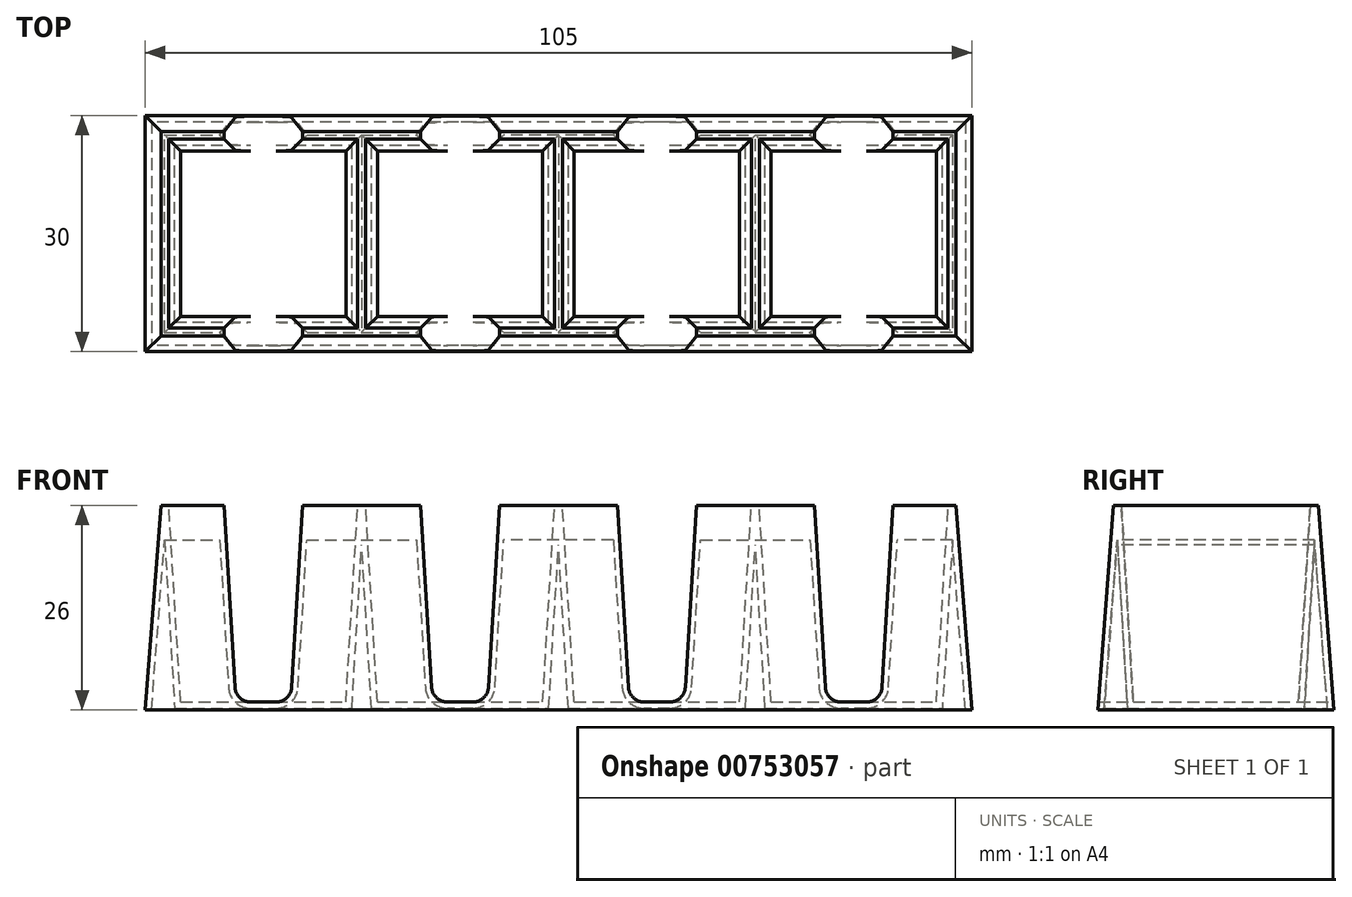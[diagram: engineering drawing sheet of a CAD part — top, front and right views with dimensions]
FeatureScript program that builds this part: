
annotation { "Feature Type Name" : "Feature", "Feature Type Description" : "" }
export const myFeature = defineFeature(function(context is Context, id is Id, definition is map)
    precondition{}
    {
        {
            var Q0;
            Q0=qCreatedBy(makeId("Right.planeOp"),FACE);
            var sketch = newSketch(context, id + "F0", { "sketchPlane" : qUnion([Q0])});
            skLineSegment(sketch, "E0.bottom", {"start": v(15, 0) * mm, "end": v(-15, 0) * mm});
            skLineSegment(sketch, "E0.top", {"start": v(13, 26) * mm, "end": v(-13, 26) * mm});
            skLineSegment(sketch, "E0.left", {"start": v(15, 0) * mm, "end": v(13, 26) * mm});
            skLineSegment(sketch, "E0.right", {"start": v(-15, 0) * mm, "end": v(-13, 26) * mm});
            skPoint(sketch, "E1", {"position": v(0, 26) * mm});
            skSolve(sketch);
        }
        {
            var Q0;
            Q0=makeQuery(id+"F0.imprint","IMPRINT",FACE,{"disambiguationData":[TD([[makeQuery(id+"F0.imprint","IMPRINT",EDGE,{"derivedFrom":sQuery(id+"F0.wireOp",EDGE,"E0.bottom")}),-1.0]])]});
            extrude(context, id + "F1", {"entities" : qUnion([Q0]), "depth" : 105 * mm, "offsetDistance" : 25 * mm});
        }
        {
            var Q0;
            Q0=qCreatedBy(makeId("Front.planeOp"),FACE);
            var sketch = newSketch(context, id + "F2", { "sketchPlane" : qUnion([Q0])});
            skLineSegment(sketch, "E2.0.0", {"start": v(0, 0) * mm, "end": v(0, 26) * mm});
            skLineSegment(sketch, "E2.0.1", {"start": v(0, 26) * mm, "end": v(105, 26) * mm});
            skLineSegment(sketch, "E2.0.2", {"start": v(105, 26) * mm, "end": v(105, 0) * mm});
            skLineSegment(sketch, "E2.0.3", {"start": v(105, 0) * mm, "end": v(0, 0) * mm});
            skLineSegment(sketch, "E3", {"start": v(0, 0) * mm, "end": v(2, 26) * mm});
            skLineSegment(sketch, "E4", {"start": v(105, 0) * mm, "end": v(103, 26) * mm});
            skLineSegment(sketch, "E5", {"start": v(103, 26) * mm, "end": v(105, 26) * mm});
            skLineSegment(sketch, "E6", {"start": v(2, 26) * mm, "end": v(0, 26) * mm});
            skLineSegment(sketch, "E7", {"start": v(-81.75, 44.93) * mm, "end": v(-86.9, 47.19) * mm});
            skSolve(sketch);
        }
        {
            var Q0;
            Q0=makeQuery(id+"F2.imprint","IMPRINT",FACE,{"disambiguationData":[TD([[makeQuery(id+"F2.imprint","IMPRINT",EDGE,{"derivedFrom":sQuery(id+"F2.wireOp",EDGE,"E2.0.0")}),-1.0]])]});
            var Q1;
            Q1=makeQuery(id+"F2.imprint","IMPRINT",FACE,{"disambiguationData":[TD([[makeQuery(id+"F2.imprint","IMPRINT",EDGE,{"derivedFrom":sQuery(id+"F2.wireOp",EDGE,"E2.0.2")}),-1.0]])]});
            extrude(context, id + "F3", {"entities" : qUnion([Q0, Q1]), "operationType" : NewBodyOperationType.REMOVE, "endBound" : BoundingType.SYMMETRIC, "oppositeDirection" : true, "depth" : 100 * mm, "offsetDistance" : 25 * mm});
        }
        {
            var Q0;
            Q0=qCreatedBy(makeId("Top.planeOp"),FACE);
            cPlane(context, id + "F4", {"entities" : qUnion([Q0]), "cplaneType" : CPlaneType.OFFSET, "offset" : 1 * mm, "width" : 150 * mm, "height" : 150 * mm});
        }
        {
            var Q0;
            Q0=qCreatedBy(id+"F4.planeOp",FACE);
            var sketch = newSketch(context, id + "F5", { "sketchPlane" : qUnion([Q0])});
            skLineSegment(sketch, "E8.0.0", {"start": v(0, -15) * mm, "end": v(0, 15) * mm});
            skLineSegment(sketch, "E8.0.1", {"start": v(0, 15) * mm, "end": v(105, 15) * mm});
            skLineSegment(sketch, "E8.0.2", {"start": v(105, 15) * mm, "end": v(105, -15) * mm});
            skLineSegment(sketch, "E8.0.3", {"start": v(105, -15) * mm, "end": v(0, -15) * mm});
            skLineSegment(sketch, "E9.bottom", {"start": v(4.5, -10.5) * mm, "end": v(25.5, -10.5) * mm});
            skLineSegment(sketch, "E9.top", {"start": v(4.5, 10.5) * mm, "end": v(25.5, 10.5) * mm});
            skLineSegment(sketch, "E9.left", {"start": v(4.5, -10.5) * mm, "end": v(4.5, 10.5) * mm});
            skLineSegment(sketch, "E9.right", {"start": v(25.5, -10.5) * mm, "end": v(25.5, 10.5) * mm});
            skLineSegment(sketch, "E10", {"start": v(0, 0) * mm, "end": v(51.63, 0) * mm, "construction": true});
            skLineSegment(sketch, "E11.1.0.0", {"start": v(50.5, -10.5) * mm, "end": v(50.5, 10.5) * mm});
            skLineSegment(sketch, "E11.1.0.1", {"start": v(29.5, -10.5) * mm, "end": v(50.5, -10.5) * mm});
            skLineSegment(sketch, "E11.1.0.2", {"start": v(29.5, -10.5) * mm, "end": v(29.5, 10.5) * mm});
            skLineSegment(sketch, "E11.1.0.3", {"start": v(29.5, 10.5) * mm, "end": v(50.5, 10.5) * mm});
            skLineSegment(sketch, "E11.2.0.0", {"start": v(75.5, -10.5) * mm, "end": v(75.5, 10.5) * mm});
            skLineSegment(sketch, "E11.2.0.1", {"start": v(54.5, -10.5) * mm, "end": v(75.5, -10.5) * mm});
            skLineSegment(sketch, "E11.2.0.2", {"start": v(54.5, -10.5) * mm, "end": v(54.5, 10.5) * mm});
            skLineSegment(sketch, "E11.2.0.3", {"start": v(54.5, 10.5) * mm, "end": v(75.5, 10.5) * mm});
            skLineSegment(sketch, "E11.3.0.0", {"start": v(100.5, -10.5) * mm, "end": v(100.5, 10.5) * mm});
            skLineSegment(sketch, "E11.3.0.1", {"start": v(79.5, -10.5) * mm, "end": v(100.5, -10.5) * mm});
            skLineSegment(sketch, "E11.3.0.2", {"start": v(79.5, -10.5) * mm, "end": v(79.5, 10.5) * mm});
            skLineSegment(sketch, "E11.3.0.3", {"start": v(79.5, 10.5) * mm, "end": v(100.5, 10.5) * mm});
            skLineSegment(sketch, "E11.direction1", {"start": v(25.5, -10.5) * mm, "end": v(50.5, -10.5) * mm, "construction": true});
            skSolve(sketch);
        }
        {
            var Q0;
            Q0=makeQuery(id+"F1.opExtrude","SWEPT_FACE",FACE,{"disambiguationData":[OSD([sQuery(id+"F0.wireOp",EDGE,"E0.top")])]});
            var sketch = newSketch(context, id + "F6", { "sketchPlane" : qUnion([Q0])});
            skLineSegment(sketch, "E12.0", {"start": v(105, 15) * mm, "end": v(105, -15) * mm});
            skLineSegment(sketch, "E12.1", {"start": v(0, 15) * mm, "end": v(105, 15) * mm});
            skLineSegment(sketch, "E12.2", {"start": v(0, -15) * mm, "end": v(0, 15) * mm});
            skLineSegment(sketch, "E12.3", {"start": v(105, -15) * mm, "end": v(0, -15) * mm});
            skLineSegment(sketch, "E13.0", {"start": v(0, 0) * mm, "end": v(51.63, 0) * mm, "construction": true});
            skLineSegment(sketch, "E14.bottom", {"start": v(3, 12) * mm, "end": v(27, 12) * mm});
            skLineSegment(sketch, "E14.top", {"start": v(3, -12) * mm, "end": v(27, -12) * mm});
            skLineSegment(sketch, "E14.left", {"start": v(3, 12) * mm, "end": v(3, -12) * mm});
            skLineSegment(sketch, "E14.right", {"start": v(27, 12) * mm, "end": v(27, -12) * mm});
            skLineSegment(sketch, "E15.0", {"start": v(2, 13) * mm, "end": v(2, -13) * mm, "construction": true});
            skLineSegment(sketch, "E16.0", {"start": v(4.5, -10.5) * mm, "end": v(4.5, 10.5) * mm, "construction": true});
            skLineSegment(sketch, "E17.1.0.0", {"start": v(28, 12) * mm, "end": v(28, -12) * mm});
            skLineSegment(sketch, "E17.1.0.1", {"start": v(28, 12) * mm, "end": v(52, 12) * mm});
            skLineSegment(sketch, "E17.1.0.2", {"start": v(52, 12) * mm, "end": v(52, -12) * mm});
            skLineSegment(sketch, "E17.1.0.3", {"start": v(28, -12) * mm, "end": v(52, -12) * mm});
            skLineSegment(sketch, "E17.2.0.0", {"start": v(53, 12) * mm, "end": v(53, -12) * mm});
            skLineSegment(sketch, "E17.2.0.1", {"start": v(53, 12) * mm, "end": v(77, 12) * mm});
            skLineSegment(sketch, "E17.2.0.2", {"start": v(77, 12) * mm, "end": v(77, -12) * mm});
            skLineSegment(sketch, "E17.2.0.3", {"start": v(53, -12) * mm, "end": v(77, -12) * mm});
            skLineSegment(sketch, "E17.3.0.0", {"start": v(78, 12) * mm, "end": v(78, -12) * mm});
            skLineSegment(sketch, "E17.3.0.1", {"start": v(78, 12) * mm, "end": v(102, 12) * mm});
            skLineSegment(sketch, "E17.3.0.2", {"start": v(102, 12) * mm, "end": v(102, -12) * mm});
            skLineSegment(sketch, "E17.3.0.3", {"start": v(78, -12) * mm, "end": v(102, -12) * mm});
            skLineSegment(sketch, "E17.direction1", {"start": v(3, -12) * mm, "end": v(28, -12) * mm, "construction": true});
            skSolve(sketch);
        }
        {
            var Q1;
            Q1=makeQuery(id+"F5.imprint","IMPRINT",FACE,{"disambiguationData":[TD([[makeQuery(id+"F5.imprint","IMPRINT",EDGE,{"derivedFrom":sQuery(id+"F5.wireOp",EDGE,"E9.bottom")}),1.0]])]});
            var Q2;
            Q2=makeQuery(id+"F6.imprint","IMPRINT",FACE,{"disambiguationData":[TD([[makeQuery(id+"F6.imprint","IMPRINT",EDGE,{"derivedFrom":sQuery(id+"F6.wireOp",EDGE,"E14.bottom")}),-1.0]])]});
            loft(context, id + "F7", {"operationType" : NewBodyOperationType.REMOVE, "sheetProfilesArray" : [{ "sheetProfileEntities" : qUnion([Q1]) }, { "sheetProfileEntities" : qUnion([Q2]) }]});
        }
        {
            var Q1;
            Q1=makeQuery(id+"F5.imprint","IMPRINT",FACE,{"disambiguationData":[TD([[makeQuery(id+"F5.imprint","IMPRINT",EDGE,{"derivedFrom":sQuery(id+"F5.wireOp",EDGE,"E11.1.0.0")}),1.0]])]});
            var Q2;
            Q2=makeQuery(id+"F6.imprint","IMPRINT",FACE,{"disambiguationData":[TD([[makeQuery(id+"F6.imprint","IMPRINT",EDGE,{"derivedFrom":sQuery(id+"F6.wireOp",EDGE,"E17.1.0.0")}),1.0]])]});
            loft(context, id + "F8", {"operationType" : NewBodyOperationType.REMOVE, "sheetProfilesArray" : [{ "sheetProfileEntities" : qUnion([Q1]) }, { "sheetProfileEntities" : qUnion([Q2]) }]});
        }
        {
            var Q1;
            Q1=makeQuery(id+"F5.imprint","IMPRINT",FACE,{"disambiguationData":[TD([[makeQuery(id+"F5.imprint","IMPRINT",EDGE,{"derivedFrom":sQuery(id+"F5.wireOp",EDGE,"E11.2.0.0")}),1.0]])]});
            var Q2;
            Q2=makeQuery(id+"F6.imprint","IMPRINT",FACE,{"disambiguationData":[TD([[makeQuery(id+"F6.imprint","IMPRINT",EDGE,{"derivedFrom":sQuery(id+"F6.wireOp",EDGE,"E17.2.0.0")}),1.0]])]});
            loft(context, id + "F9", {"operationType" : NewBodyOperationType.REMOVE, "sheetProfilesArray" : [{ "sheetProfileEntities" : qUnion([Q1]) }, { "sheetProfileEntities" : qUnion([Q2]) }]});
        }
        {
            var Q1;
            Q1=makeQuery(id+"F5.imprint","IMPRINT",FACE,{"disambiguationData":[TD([[makeQuery(id+"F5.imprint","IMPRINT",EDGE,{"derivedFrom":sQuery(id+"F5.wireOp",EDGE,"E11.3.0.0")}),1.0]])]});
            var Q2;
            Q2=makeQuery(id+"F6.imprint","IMPRINT",FACE,{"disambiguationData":[TD([[makeQuery(id+"F6.imprint","IMPRINT",EDGE,{"derivedFrom":sQuery(id+"F6.wireOp",EDGE,"E17.3.0.0")}),1.0]])]});
            loft(context, id + "F10", {"operationType" : NewBodyOperationType.REMOVE, "sheetProfilesArray" : [{ "sheetProfileEntities" : qUnion([Q1]) }, { "sheetProfileEntities" : qUnion([Q2]) }]});
        }
        {
            var Q0;
            Q0=qCreatedBy(makeId("Front.planeOp"),FACE);
            var sketch = newSketch(context, id + "F11", { "sketchPlane" : qUnion([Q0])});
            skPoint(sketch, "E18.1", {"position": v(4.5, 1) * mm});
            skPoint(sketch, "E18.2", {"position": v(25.5, 1) * mm});
            skPoint(sketch, "E18.3", {"position": v(27, 26) * mm});
            skLineSegment(sketch, "E19", {"start": v(25.5, 1) * mm, "end": v(27, 26) * mm, "construction": true});
            skLineSegment(sketch, "E20", {"start": v(25.5, 1) * mm, "end": v(4.5, 1) * mm});
            skLineSegment(sketch, "E21", {"start": v(16.62, 1) * mm, "end": v(13.38, 1) * mm, "construction": true});
            skPoint(sketch, "E22.0", {"position": v(3, 26) * mm});
            skLineSegment(sketch, "E23", {"start": v(3, 26) * mm, "end": v(27, 26) * mm, "construction": true});
            skLineSegment(sketch, "E24", {"start": v(3, 26) * mm, "end": v(4.5, 1) * mm, "construction": true});
            skLineSegment(sketch, "E25", {"start": v(15, 26) * mm, "end": v(15, 1) * mm, "construction": true});
            skLineSegment(sketch, "E26", {"start": v(10, 26) * mm, "end": v(20, 26) * mm});
            skLineSegment(sketch, "E27", {"start": v(11.39, 2.88) * mm, "end": v(10, 26) * mm});
            skLineSegment(sketch, "E28", {"start": v(20, 26) * mm, "end": v(18.61, 2.88) * mm});
            skLineSegment(sketch, "E29", {"start": v(11.5, 1) * mm, "end": v(18.5, 1) * mm});
            skArc(sketch, "E30.filletArc", {"start": v(11.39, 2.88) * mm, "mid": v(12.01, 1.54) * mm, "end": v(13.38, 1) * mm});
            skArc(sketch, "E31.filletArc", {"start": v(16.62, 1) * mm, "mid": v(17.99, 1.54) * mm, "end": v(18.61, 2.88) * mm});
            skLineSegment(sketch, "E32.1.0.0", {"start": v(40, 26) * mm, "end": v(40, 1) * mm, "construction": true});
            skLineSegment(sketch, "E32.1.0.1", {"start": v(45, 26) * mm, "end": v(43.61, 2.88) * mm});
            skLineSegment(sketch, "E32.1.0.2", {"start": v(35, 26) * mm, "end": v(45, 26) * mm});
            skLineSegment(sketch, "E32.1.0.3", {"start": v(36.39, 2.88) * mm, "end": v(35, 26) * mm});
            skLineSegment(sketch, "E32.1.0.4", {"start": v(41.62, 1) * mm, "end": v(38.38, 1) * mm, "construction": true});
            skLineSegment(sketch, "E32.1.0.5", {"start": v(36.5, 1) * mm, "end": v(43.5, 1) * mm});
            skArc(sketch, "E32.1.0.6", {"start": v(36.39, 2.88) * mm, "mid": v(37.01, 1.54) * mm, "end": v(38.38, 1) * mm});
            skArc(sketch, "E32.1.0.7", {"start": v(41.62, 1) * mm, "mid": v(42.99, 1.54) * mm, "end": v(43.61, 2.88) * mm});
            skLineSegment(sketch, "E32.2.0.0", {"start": v(65, 26) * mm, "end": v(65, 1) * mm, "construction": true});
            skLineSegment(sketch, "E32.2.0.1", {"start": v(70, 26) * mm, "end": v(68.61, 2.88) * mm});
            skLineSegment(sketch, "E32.2.0.2", {"start": v(60, 26) * mm, "end": v(70, 26) * mm});
            skLineSegment(sketch, "E32.2.0.3", {"start": v(61.39, 2.88) * mm, "end": v(60, 26) * mm});
            skLineSegment(sketch, "E32.2.0.4", {"start": v(66.62, 1) * mm, "end": v(63.38, 1) * mm, "construction": true});
            skLineSegment(sketch, "E32.2.0.5", {"start": v(61.5, 1) * mm, "end": v(68.5, 1) * mm});
            skArc(sketch, "E32.2.0.6", {"start": v(61.39, 2.88) * mm, "mid": v(62.01, 1.54) * mm, "end": v(63.38, 1) * mm});
            skArc(sketch, "E32.2.0.7", {"start": v(66.62, 1) * mm, "mid": v(67.99, 1.54) * mm, "end": v(68.61, 2.88) * mm});
            skLineSegment(sketch, "E32.3.0.0", {"start": v(90, 26) * mm, "end": v(90, 1) * mm, "construction": true});
            skLineSegment(sketch, "E32.3.0.1", {"start": v(95, 26) * mm, "end": v(93.61, 2.88) * mm});
            skLineSegment(sketch, "E32.3.0.2", {"start": v(85, 26) * mm, "end": v(95, 26) * mm});
            skLineSegment(sketch, "E32.3.0.3", {"start": v(86.39, 2.88) * mm, "end": v(85, 26) * mm});
            skLineSegment(sketch, "E32.3.0.4", {"start": v(91.62, 1) * mm, "end": v(88.38, 1) * mm, "construction": true});
            skLineSegment(sketch, "E32.3.0.5", {"start": v(86.5, 1) * mm, "end": v(93.5, 1) * mm});
            skArc(sketch, "E32.3.0.6", {"start": v(86.39, 2.88) * mm, "mid": v(87.01, 1.54) * mm, "end": v(88.38, 1) * mm});
            skArc(sketch, "E32.3.0.7", {"start": v(91.62, 1) * mm, "mid": v(92.99, 1.54) * mm, "end": v(93.61, 2.88) * mm});
            skLineSegment(sketch, "E32.direction1", {"start": v(11.5, 1) * mm, "end": v(36.5, 1) * mm, "construction": true});
            skSolve(sketch);
        }
        {
            var Q0;
            Q0=makeQuery(id+"F11.imprint","IMPRINT",FACE,{"disambiguationData":[TD([[makeQuery(id+"F11.imprint","IMPRINT",EDGE,{"derivedFrom":sQuery(id+"F11.wireOp",EDGE,"E26")}),-1.0]])]});
            var Q1;
            Q1=makeQuery(id+"F11.imprint","IMPRINT",FACE,{"disambiguationData":[TD([[makeQuery(id+"F11.imprint","IMPRINT",EDGE,{"derivedFrom":sQuery(id+"F11.wireOp",EDGE,"E32.1.0.1")}),-1.0]])]});
            var Q2;
            Q2=makeQuery(id+"F11.imprint","IMPRINT",FACE,{"disambiguationData":[TD([[makeQuery(id+"F11.imprint","IMPRINT",EDGE,{"derivedFrom":sQuery(id+"F11.wireOp",EDGE,"E32.2.0.1")}),-1.0]])]});
            var Q3;
            Q3=makeQuery(id+"F11.imprint","IMPRINT",FACE,{"disambiguationData":[TD([[makeQuery(id+"F11.imprint","IMPRINT",EDGE,{"derivedFrom":sQuery(id+"F11.wireOp",EDGE,"E32.3.0.1")}),-1.0]])]});
            extrude(context, id + "F12", {"entities" : qUnion([Q0, Q1, Q2, Q3]), "operationType" : NewBodyOperationType.REMOVE, "endBound" : BoundingType.SYMMETRIC, "depth" : 50 * mm, "offsetDistance" : 25 * mm});
        }
        {
            var Q0;
            Q0=makeQuery(id+"F1.opExtrude","SWEPT_FACE",FACE,{"disambiguationData":[OSD([sQuery(id+"F0.wireOp",EDGE,"E0.bottom")])]});
            shell(context, id + "F13", {"entities" : qUnion([Q0]), "thickness" : 0.8 * mm});
        }
    });
